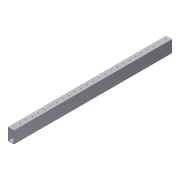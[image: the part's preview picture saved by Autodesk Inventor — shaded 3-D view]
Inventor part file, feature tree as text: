
AUTODESK INVENTOR PART (.ipt)
format: ipt  version: 2015 (Build 190159000, 159)  size: 352,768 bytes
history: native  units: in
note: dims shown in document units (in); Inventor stores cm internally (conversion verified against a paired STEP export)
features: other x3, extrude x3, sketch x3, pattern_linear x1
ambient origin geometry x8: Origin, YZ Plane, XZ Plane, XY Plane, X Axis, Y Axis, Z Axis, Center Point
bodies: Solid1 (feature_tree)
feature tree (10):
  other  "Blocks"
  extrude  "Extrusion1"  Depth=0.05in
  extrude  "Extrusion2"  Depth=0.164in
  pattern_linear  "Rectangular Pattern1"  Spacing1=59.0in  [1 undecoded]
  extrude  "Extrusion3"  Depth=2.0in
  sketch  "Sketch1"  dims[d0=60.0in d1=0.0in d11=0.05in]
  other  "VersaFrameProfile"
  sketch  "Sketch2"  dims[d12=0.164in d13=0.164in]
  sketch  "Sketch3"  dims[d15=1.0in d16=59.0in d17=0.0in d18=11.811in d20=2.0in d21=1.0in d22=2.0in d24=0.0in]
  other  "VersaFrameProfile:1"
note: 1 required parameter value undecoded (feature->parameter linkage not recoverable at this tier; creation-order binding heuristic only, values carry confidence <= 0.55)
